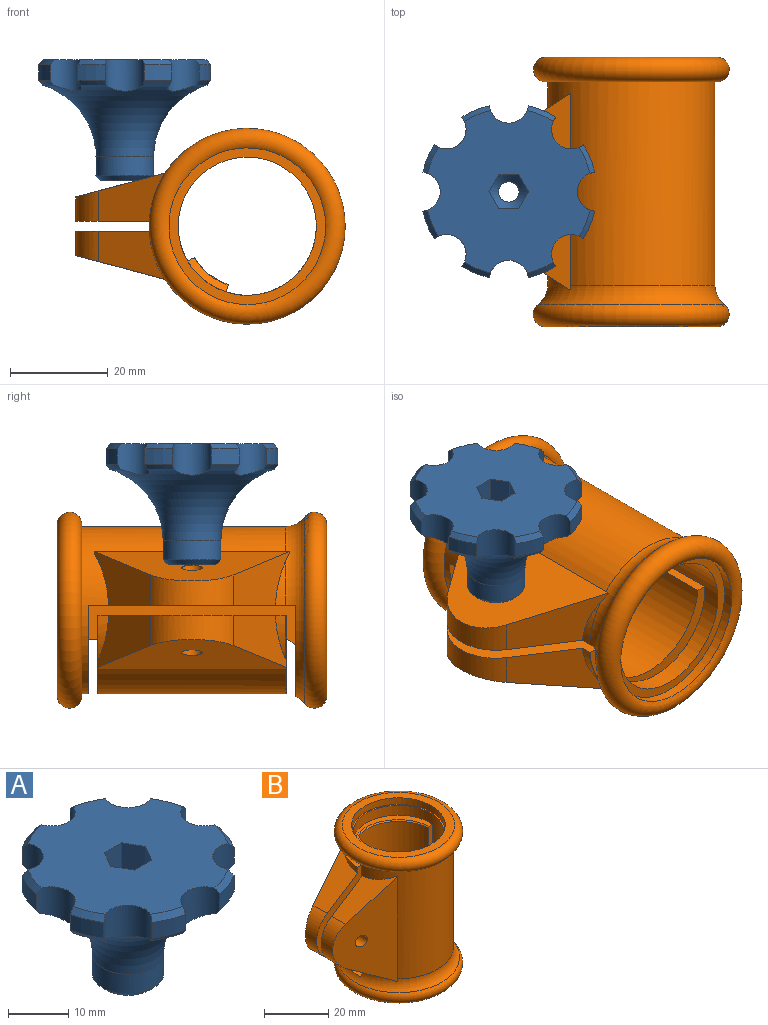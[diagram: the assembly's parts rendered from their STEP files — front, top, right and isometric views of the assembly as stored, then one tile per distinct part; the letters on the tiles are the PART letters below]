
ASSEMBLY  parts=2 mates=1
PART A: 45 faces, bbox 45.4x45.4x30.6 mm
  f0: plane 33.17x33.17mm, normal (0,0,1), area 736.5mm2, adj f2,f5,f8,f11,f14,f17,f21,f27
  f1: cone r=18mm half-angle=37.9deg, axis (0,0,1), area 7.3mm2, adj f23,f24,f36,f43
  f2: cone r=17mm half-angle=45deg, axis (0,0,-1), area 8.4mm2, adj f0,f24,f36,f43
  f3: cylinder r=18mm len=5.63mm, axis (0,0,1), area 19.6mm2, adj f4,f5,f42,f43
  f4: cone r=18mm half-angle=37.9deg, axis (0,0,1), area 7.3mm2, adj f3,f23,f42,f43
  f5: cone r=17mm half-angle=45deg, axis (0,0,-1), area 8.4mm2, adj f0,f3,f42,f43
  f6: cylinder r=18mm len=5.63mm, axis (0,0,1), area 19.6mm2, adj f7,f8,f41,f42
  f7: cone r=18mm half-angle=37.9deg, axis (0,0,1), area 7.3mm2, adj f6,f23,f41,f42
  f8: cone r=17mm half-angle=45deg, axis (0,0,-1), area 8.4mm2, adj f0,f6,f41,f42
  f9: cylinder r=18mm len=5.63mm, axis (0,0,1), area 19.6mm2, adj f10,f11,f40,f41
  f10: cone r=18mm half-angle=37.9deg, axis (0,0,1), area 7.3mm2, adj f9,f23,f40,f41
  f11: cone r=17mm half-angle=45deg, axis (0,0,-1), area 8.4mm2, adj f0,f9,f40,f41
  f12: cylinder r=18mm len=5.63mm, axis (0,0,1), area 19.6mm2, adj f13,f14,f39,f40
  f13: cone r=18mm half-angle=37.9deg, axis (0,0,1), area 7.3mm2, adj f12,f23,f39,f40
  f14: cone r=17mm half-angle=45deg, axis (0,0,-1), area 8.4mm2, adj f0,f12,f39,f40
  f15: cylinder r=18mm len=5.63mm, axis (0,0,1), area 19.6mm2, adj f16,f17,f38,f39
  f16: cone r=18mm half-angle=37.9deg, axis (0,0,1), area 7.3mm2, adj f15,f23,f38,f39
  f17: cone r=17mm half-angle=45deg, axis (0,0,-1), area 8.4mm2, adj f0,f15,f38,f39
  f18: cylinder r=18mm len=5.63mm, axis (0,0,1), area 19.6mm2, adj f20,f21,f37,f38
  f19: cylinder r=18mm len=5.63mm, axis (0,0,1), area 19.6mm2, adj f34,f35,f36,f37
  f20: cone r=18mm half-angle=37.9deg, axis (0,0,1), area 7.3mm2, adj f18,f23,f37,f38
  f21: cone r=17mm half-angle=45deg, axis (0,0,-1), area 8.4mm2, adj f0,f18,f37,f38
  f22: cylinder r=2.1mm len=16.72mm, axis (0,0,1), area 220.6mm2, adj f25,f44
  f23: torus R=20.9mm, axis (0,0,1), area 1085.1mm2, adj f1,f4,f7,f10,f13,f16,f20,f26
  f24: cylinder r=18mm len=5.63mm, axis (0,0,1), area 19.6mm2, adj f1,f2,f36,f43
  f25: plane 9.8x9.8mm, normal (0,0,-1), area 61.6mm2, adj f22,f33
  f26: cylinder r=5.9mm len=11.8mm, axis (0,0,1), area 148.3mm2, adj f23,f33
  f27: plane 6.61x3.5mm, normal (0.87,-0.5,0), area 25.9mm2, adj f0,f28,f32,f44
  f28: plane 6.61x3.5mm, normal (0.87,0.5,0), area 25.9mm2, adj f0,f27,f29,f44
  f29: plane 6.61x4.04mm, normal (0,1,0), area 25.9mm2, adj f0,f28,f30,f44
  f30: plane 6.8x3.69mm, normal (-0.87,0.5,0), area 25.9mm2, adj f0,f29,f31,f44
  f31: plane 6.61x3.5mm, normal (-0.87,-0.5,0), area 25.9mm2, adj f0,f30,f32,f44
  f32: plane 6.61x4.04mm, normal (0,-1,0), area 25.9mm2, adj f0,f27,f31,f44
  f33: cone r=5.9mm half-angle=45deg, axis (0,0,1), area 48mm2, adj f25,f26
  f34: cone r=18mm half-angle=37.9deg, axis (0,0,1), area 7.3mm2, adj f19,f23,f36,f37
  f35: cone r=17mm half-angle=45deg, axis (0,0,-1), area 8.4mm2, adj f0,f19,f36,f37
  f36: cylinder r=4mm len=7.95mm, axis (0,0,1), area 65.9mm2, adj f0,f1,f2,f19,f23,f24,f34,f35
  f37: cylinder r=4mm len=6.5mm, axis (0,0,1), area 65.9mm2, adj f0,f18,f19,f20,f21,f23,f34,f35
  f38: cylinder r=4mm len=7.95mm, axis (0,0,1), area 65.9mm2, adj f0,f15,f16,f17,f18,f20,f21,f23
  f39: cylinder r=4mm len=6.5mm, axis (0,0,1), area 65.9mm2, adj f0,f12,f13,f14,f15,f16,f17,f23
  f40: cylinder r=4mm len=7.95mm, axis (0,0,1), area 64.9mm2, adj f0,f9,f10,f11,f12,f13,f14,f23
  f41: cylinder r=4mm len=6.5mm, axis (0,0,1), area 65.9mm2, adj f0,f6,f7,f8,f9,f10,f11,f23
  f42: cylinder r=4mm len=7.95mm, axis (0,0,1), area 65.9mm2, adj f0,f3,f4,f5,f6,f7,f8,f23
  f43: cylinder r=4mm len=6.5mm, axis (0,0,1), area 65.9mm2, adj f0,f1,f2,f3,f4,f5,f23,f24
  f44: cone r=2.1mm half-angle=45deg, axis (0,0,1), area 40.5mm2, adj f22,f27,f28,f29,f30,f31,f32
PART B: 74 faces, bbox 61.4x50.3x57.4 mm
  f0: cylinder r=12.5mm len=6.92mm, axis (0,0,1), area 2.7mm2, adj f48,f49,f71,f72
  f1: cylinder r=12.5mm len=6.92mm, axis (0,0,1), area 2.7mm2, adj f48,f49,f69,f70
  f2: cylinder r=12.5mm len=6.92mm, axis (0,0,1), area 2.7mm2, adj f48,f49,f67,f68
  f3: cylinder r=12.5mm len=6.92mm, axis (0,0,1), area 2.7mm2, adj f48,f49,f65,f66
  f4: cylinder r=12.5mm len=6.92mm, axis (0,0,1), area 2.7mm2, adj f48,f49,f63,f64
  f5: cylinder r=12.5mm len=6.92mm, axis (0,0,1), area 2.7mm2, adj f48,f49,f61,f62
  f6: cylinder r=12.5mm len=6.92mm, axis (0,0,1), area 2.7mm2, adj f48,f49,f59,f60
  f7: cylinder r=12.5mm len=6.92mm, axis (0,0,1), area 2.7mm2, adj f48,f49,f57,f58
  f8: cylinder r=12.5mm len=6.92mm, axis (0,0,1), area 2.7mm2, adj f48,f49,f55,f56
  f9: cylinder r=12.5mm len=6.92mm, axis (0,0,1), area 2.7mm2, adj f48,f49,f53,f54
  f10: cylinder r=17.1mm len=44.08mm, axis (0,0,-1), area 3663.1mm2, adj f14,f22,f26,f27,f28,f30,f36,f42
  f11: cylinder r=17.1mm len=8.92mm, axis (0,0,-1), area 9.7mm2, adj f13,f33,f38
  f12: cylinder r=17.1mm len=8.92mm, axis (0,0,-1), area 9.7mm2, adj f14,f30,f43
  f13: torus R=22.1mm, axis (0,0,-1), area 1.5mm2, adj f11,f32,f33,f38
  f14: torus R=22.1mm, axis (0,0,-1), area 404.2mm2, adj f10,f12,f24,f28,f29,f30,f32,f36
  f15: plane 32x32mm, normal (0,0,-1), area 179.7mm2, adj f18,f25
  f16: cylinder r=17.1mm len=9.25mm, axis (0,0,-1), area 10.9mm2, adj f27,f33,f37
  f17: plane 29.2x29.2mm, normal (0,0,1), area 45.1mm2, adj f18,f23
  f18: cylinder r=14.1mm len=50mm, axis (0,0,-1), area 2463.8mm2, adj f15,f17,f26,f29,f30,f31
  f19: plane 35x35mm, normal (0,0,1), area 292.5mm2, adj f20,f23
  f20: torus R=17.5mm, axis (0,0,1), area 942.1mm2, adj f19,f21
  f21: cylinder r=17.5mm len=35mm, axis (0,0,1), area 274.9mm2, adj f20,f22
  f22: plane 35x35mm, normal (0,0,-1), area 43.5mm2, adj f10,f21
  f23: cylinder r=14.6mm len=29.2mm, axis (0,0,1), area 229.3mm2, adj f17,f19
  f24: torus R=17.5mm, axis (0,0,1), area 921.4mm2, adj f14,f25
  f25: cylinder r=16mm len=32mm, axis (0,0,1), area 201.1mm2, adj f15,f24
  f26: plane 33.1x18.1mm, normal (0,0,-1), area 147.5mm2, adj f10,f18,f28,f30,f31
  f27: plane 33.07x16.1mm, normal (0,0,1), area 121.5mm2, adj f10,f16,f28,f33,f34,f36,f37,f39
  f28: plane 42.46x8.3mm, normal (-1,0,0), area 106mm2, adj f10,f14,f26,f27,f29,f31,f32,f34
  f29: plane 33.59x18.59mm, normal (0,0,1), area 171.2mm2, adj f14,f18,f28,f30,f31
  f30: plane 42.48x20.95mm, normal (0,1,0), area 508.1mm2, adj f10,f12,f14,f18,f26,f29,f43,f44
  f31: plane 42.46x1.94mm, normal (0,1,0), area 82.2mm2, adj f18,f26,f28,f29
  f32: plane 33.09x16.21mm, normal (0,0,-1), area 138.9mm2, adj f13,f14,f28,f33,f34,f35,f36,f38
  f33: plane 38.46x20.94mm, normal (0,-1,0), area 495.6mm2, adj f11,f13,f16,f27,f32,f35,f37,f38
  f34: plane 38.46x1.94mm, normal (0,-1,0), area 74.4mm2, adj f27,f28,f32,f35,f51
  f35: cylinder r=14.1mm len=38.06mm, axis (0,0,-1), area 1413.5mm2, adj f32,f33,f34,f48,f49,f50,f51
  f36: plane 38.47x0.34mm, normal (1,0,0), area 12.7mm2, adj f10,f14,f27,f32,f39
  f37: plane 17.62x11.71mm, normal (-0.54,0,0.84), area 144mm2, adj f16,f27,f33,f39,f40
  f38: plane 17.56x11.65mm, normal (-0.54,0,-0.84), area 144mm2, adj f11,f13,f32,f33,f39,f40
  f39: plane 40.91x24.95mm, normal (-0.26,0.97,0), area 567.8mm2, adj f27,f32,f36,f37,f38,f40,f41
  f40: cylinder r=10mm len=16.79mm, axis (0,-1,0), area 123.5mm2, adj f33,f37,f38,f39
  f41: cylinder r=2.1mm len=7.65mm, axis (0,-1,0), area 97.2mm2, adj f33,f39
  f42: plane 40.05x0.38mm, normal (1,0,0), area 13.2mm2, adj f10,f14,f43,f44,f47
  f43: plane 18.75x12.42mm, normal (-0.54,0,-0.84), area 145.1mm2, adj f12,f14,f30,f42,f45,f47
  f44: plane 19.14x12.81mm, normal (-0.54,0,0.84), area 145.2mm2, adj f10,f30,f42,f45,f47
  f45: cylinder r=10mm len=16.79mm, axis (0,1,0), area 123.5mm2, adj f30,f43,f44,f47
  f46: cylinder r=2.1mm len=7.65mm, axis (0,1,0), area 97.2mm2, adj f30,f47
  f47: plane 42.45x24.95mm, normal (-0.26,-0.97,0), area 568.8mm2, adj f42,f43,f44,f45,f46
  f48: plane 19.2x1.52mm, normal (0.95,0.31,0), area 24.2mm2, adj f0,f1,f2,f3,f4,f5,f6,f7
  f49: plane 19.2x1.38mm, normal (-0.51,-0.86,0), area 24.2mm2, adj f0,f1,f2,f3,f4,f5,f6,f7
  f50: cone r=12.5mm half-angle=45deg, axis (0,0,-1), area 20.5mm2, adj f35,f48,f49,f73
  f51: cone r=14.5mm half-angle=45deg, axis (0,0,1), area 46.1mm2, adj f27,f33,f34,f35,f48,f49,f52
  f52: cone r=12.5mm half-angle=45deg, axis (0,0,-1), area 7.9mm2, adj f48,f49,f51,f53
  f53: cone r=13.1mm half-angle=45deg, axis (0,0,1), area 7.9mm2, adj f9,f48,f49,f52
  f54: cone r=12.5mm half-angle=45deg, axis (0,0,-1), area 7.9mm2, adj f9,f48,f49,f55
  f55: cone r=13.1mm half-angle=45deg, axis (0,0,1), area 7.9mm2, adj f8,f48,f49,f54
  f56: cone r=12.5mm half-angle=45deg, axis (0,0,-1), area 7.9mm2, adj f8,f48,f49,f57
  f57: cone r=13.1mm half-angle=45deg, axis (0,0,1), area 7.9mm2, adj f7,f48,f49,f56
  f58: cone r=12.5mm half-angle=45deg, axis (0,0,-1), area 7.9mm2, adj f7,f48,f49,f59
  f59: cone r=13.1mm half-angle=45deg, axis (0,0,1), area 7.9mm2, adj f6,f48,f49,f58
  f60: cone r=12.5mm half-angle=45deg, axis (0,0,-1), area 7.9mm2, adj f6,f48,f49,f61
  f61: cone r=13.1mm half-angle=45deg, axis (0,0,1), area 7.9mm2, adj f5,f48,f49,f60
  f62: cone r=12.5mm half-angle=45deg, axis (0,0,-1), area 7.9mm2, adj f5,f48,f49,f63
  f63: cone r=13.1mm half-angle=45deg, axis (0,0,1), area 7.9mm2, adj f4,f48,f49,f62
  f64: cone r=12.5mm half-angle=45deg, axis (0,0,-1), area 7.9mm2, adj f4,f48,f49,f65
  f65: cone r=13.1mm half-angle=45deg, axis (0,0,1), area 7.9mm2, adj f3,f48,f49,f64
  f66: cone r=12.5mm half-angle=45deg, axis (0,0,-1), area 7.9mm2, adj f3,f48,f49,f67
  f67: cone r=13.1mm half-angle=45deg, axis (0,0,1), area 7.9mm2, adj f2,f48,f49,f66
  f68: cone r=12.5mm half-angle=45deg, axis (0,0,-1), area 7.9mm2, adj f2,f48,f49,f69
  f69: cone r=13.1mm half-angle=45deg, axis (0,0,1), area 7.9mm2, adj f1,f48,f49,f68
  f70: cone r=12.5mm half-angle=45deg, axis (0,0,-1), area 7.9mm2, adj f1,f48,f49,f71
  f71: cone r=13.1mm half-angle=45deg, axis (0,0,1), area 7.9mm2, adj f0,f48,f49,f70
  f72: cone r=12.5mm half-angle=45deg, axis (0,0,-1), area 7.9mm2, adj f0,f48,f49,f73
  f73: cone r=13.1mm half-angle=45deg, axis (0,0,1), area 6.6mm2, adj f48,f49,f50,f72
PLACE A t=(-39.83,-41.45,0.61)mm
PLACE B rot(axis=(-1,0,0),90deg) t=(-14.83,-41.45,-8.65)mm
MATE revolute B.f41 <-> A.f1  axis (0,0,-1) through (-39.83,-41.45,0.61)mm
